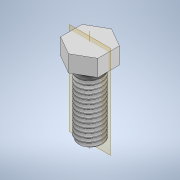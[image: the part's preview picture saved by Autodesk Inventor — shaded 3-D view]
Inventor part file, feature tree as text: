
AUTODESK INVENTOR PART (.ipt)
format: ipt  version: 2021 (Build 250183000, 183)  size: 456,704 bytes
history: native  units: in
note: dims shown in document units (in); Inventor stores cm internally (conversion verified against a paired STEP export)
features: extrude x2, sketch x2, helix x1
ambient origin geometry x8: Origin, YZ Plane, XZ Plane, XY Plane, X Axis, Y Axis, Z Axis, Center Point
bodies: Solid1 (feature_tree)
feature tree (5):
  extrude  "Extrusion1"  Depth=1.0in TaperAngle=0.0deg
  extrude  "Extrusion3"  Depth=0.1496in TaperAngle=0.0deg
  helix  "Coil13"  [1 undecoded]
  sketch  "Sketch1"  dims[d0=0.3737in d1=1.0in d2=0.0in]
  sketch  "Sketch14"  dims[d149=0.5625in d150=0.25in d151=0.0in d159=0.0625in d160=1.0in d161=0.3937in d162=0.0in d163=90.0deg d164=90.0deg d165=0.0in d166=0.0in d167=60.0deg d168=60.0deg d169=0.0078in d170=0.1496in d171=0.0in d172=60.0deg]
note: 1 required parameter value undecoded (feature->parameter linkage not recoverable at this tier; creation-order binding heuristic only, values carry confidence <= 0.55)
